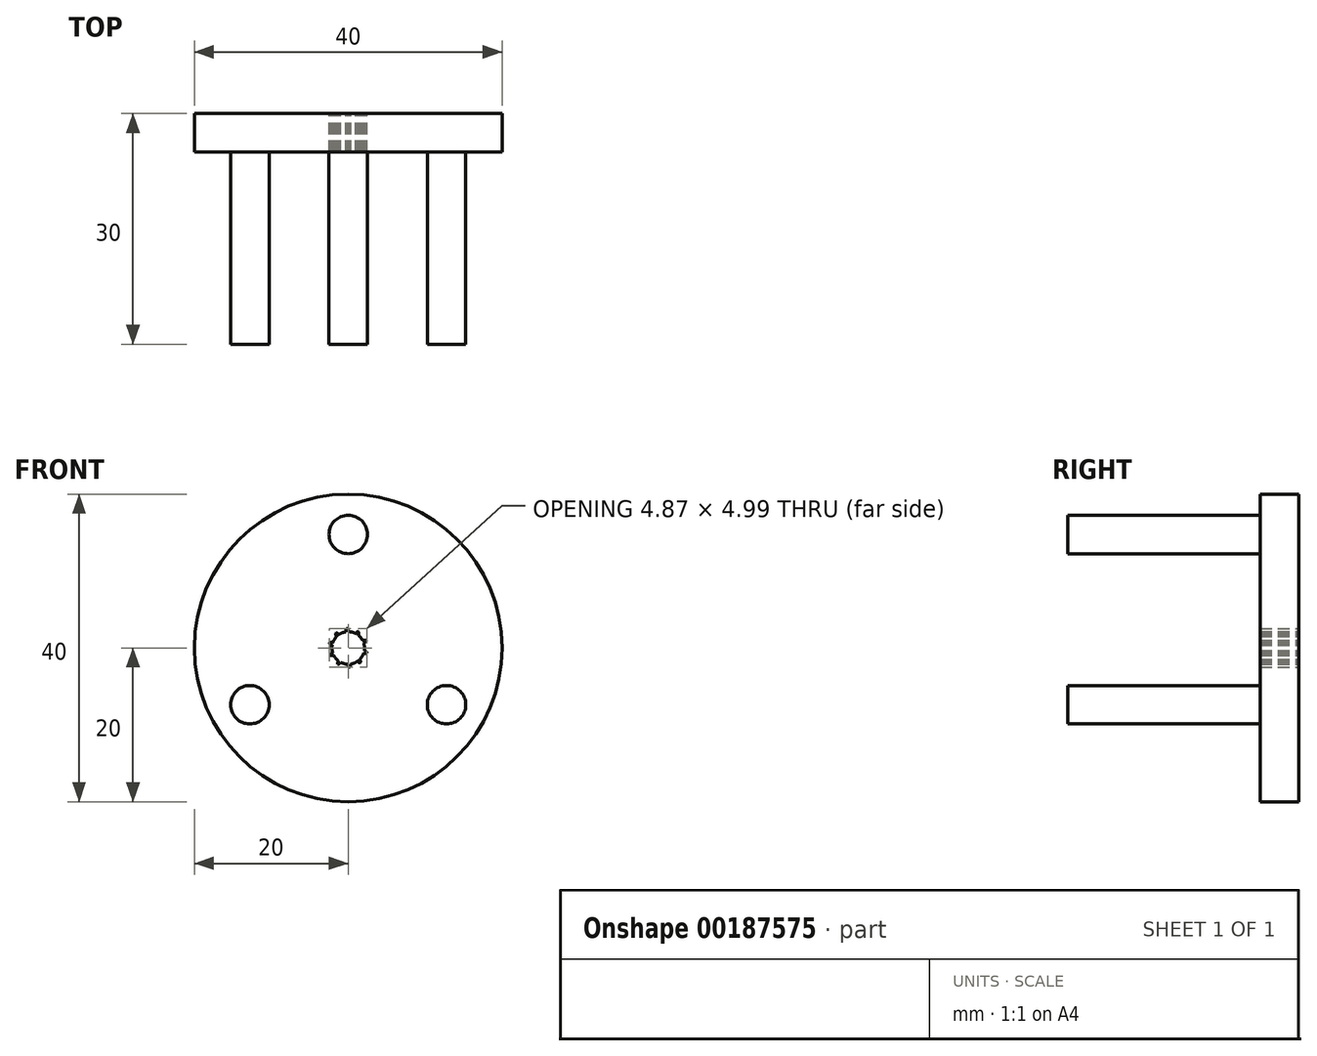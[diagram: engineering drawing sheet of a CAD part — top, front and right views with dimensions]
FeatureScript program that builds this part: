
annotation { "Feature Type Name" : "Feature", "Feature Type Description" : "" }
export const myFeature = defineFeature(function(context is Context, id is Id, definition is map)
    precondition{}
    {
        {
            var Q0;
            Q0=qCreatedBy(makeId("Front.planeOp"),FACE);
            var sketch = newSketch(context, id + "F0", { "sketchPlane" : qUnion([Q0])});
            skCircle(sketch, "E0", {"center": v(0, 0) * mm, "radius": 20 * mm});
            skCircle(sketch, "E1", {"center": v(0, 0) * mm, "radius": 2.12 * mm});
            skCircle(sketch, "E2", {"center": v(0, 0) * mm, "radius": 2.31 * mm, "construction": true});
            skCircle(sketch, "E3", {"center": v(0, 0) * mm, "radius": 2.5 * mm, "construction": true});
            skLineSegment(sketch, "E4", {"start": v(0, 0) * mm, "end": v(0, 3) * mm, "construction": true});
            skLineSegment(sketch, "E5", {"start": v(0, 0) * mm, "end": v(-0.2, 3) * mm, "construction": true});
            skLineSegment(sketch, "E6", {"start": v(0, 2.31) * mm, "end": v(-2.48, 2.31) * mm, "construction": true});
            skLineSegment(sketch, "E7", {"start": v(0, 2.31) * mm, "end": v(-2.45, 1.42) * mm, "construction": true});
            skCircle(sketch, "E8", {"center": v(0, 2.31) * mm, "radius": 0.57 * mm, "construction": true});
            skCircle(sketch, "E9", {"center": v(0, 0) * mm, "radius": 2.17 * mm, "construction": true});
            skCircle(sketch, "E10", {"center": v(-0.54, 2.1) * mm, "radius": 0.57 * mm, "construction": true});
            skArc(sketch, "E11", {"start": v(0, 2.31) * mm, "mid": v(-0.05, 2.4) * mm, "end": v(-0.12, 2.5) * mm});
            skArc(sketch, "E12", {"start": v(0.04, 2.11) * mm, "mid": v(0.03, 2.21) * mm, "end": v(0, 2.31) * mm});
            skArc(sketch, "E13.MirrorCS", {"start": v(-0.3, 2.3) * mm, "mid": v(-0.27, 2.4) * mm, "end": v(-0.2, 2.5) * mm});
            skArc(sketch, "E14.MirrorCS", {"start": v(-0.31, 2.1) * mm, "mid": v(-0.32, 2.2) * mm, "end": v(-0.3, 2.3) * mm});
            skLineSegment(sketch, "E15", {"start": v(-0.2, 2.5) * mm, "end": v(-0.12, 2.5) * mm});
            skArc(sketch, "E16.1.0", {"start": v(1.1, 2.03) * mm, "mid": v(1.2, 2.1) * mm, "end": v(1.3, 2.14) * mm});
            skArc(sketch, "E16.1.1", {"start": v(0.98, 1.88) * mm, "mid": v(1.03, 1.96) * mm, "end": v(1.1, 2.03) * mm});
            skLineSegment(sketch, "E16.1.2", {"start": v(1.3, 2.14) * mm, "end": v(1.37, 2.09) * mm});
            skArc(sketch, "E16.1.3", {"start": v(1.36, 1.87) * mm, "mid": v(1.38, 1.98) * mm, "end": v(1.37, 2.09) * mm});
            skArc(sketch, "E16.1.4", {"start": v(1.27, 1.69) * mm, "mid": v(1.32, 1.77) * mm, "end": v(1.36, 1.87) * mm});
            skArc(sketch, "E16.2.0", {"start": v(2.08, 1) * mm, "mid": v(2.2, 1) * mm, "end": v(2.3, 0.97) * mm});
            skArc(sketch, "E16.2.1", {"start": v(1.9, 0.94) * mm, "mid": v(1.99, 0.98) * mm, "end": v(2.08, 1) * mm});
            skLineSegment(sketch, "E16.2.2", {"start": v(2.3, 0.97) * mm, "end": v(2.34, 0.88) * mm});
            skArc(sketch, "E16.2.3", {"start": v(2.2, 0.71) * mm, "mid": v(2.28, 0.8) * mm, "end": v(2.34, 0.88) * mm});
            skArc(sketch, "E16.2.4", {"start": v(2.02, 0.62) * mm, "mid": v(2.11, 0.66) * mm, "end": v(2.2, 0.71) * mm});
            skArc(sketch, "E16.3.0", {"start": v(2.27, -0.42) * mm, "mid": v(2.36, -0.49) * mm, "end": v(2.43, -0.57) * mm});
            skArc(sketch, "E16.3.1", {"start": v(2.09, -0.35) * mm, "mid": v(2.18, -0.38) * mm, "end": v(2.27, -0.42) * mm});
            skLineSegment(sketch, "E16.3.2", {"start": v(2.43, -0.57) * mm, "end": v(2.41, -0.66) * mm});
            skArc(sketch, "E16.3.3", {"start": v(2.2, -0.71) * mm, "mid": v(2.3, -0.7) * mm, "end": v(2.41, -0.66) * mm});
            skArc(sketch, "E16.3.4", {"start": v(2, -0.69) * mm, "mid": v(2.1, -0.71) * mm, "end": v(2.2, -0.71) * mm});
            skArc(sketch, "E16.4.0", {"start": v(1.6, -1.68) * mm, "mid": v(1.62, -1.78) * mm, "end": v(1.63, -1.9) * mm});
            skArc(sketch, "E16.4.1", {"start": v(1.48, -1.5) * mm, "mid": v(1.54, -1.59) * mm, "end": v(1.6, -1.68) * mm});
            skLineSegment(sketch, "E16.4.2", {"start": v(1.63, -1.9) * mm, "end": v(1.56, -1.95) * mm});
            skArc(sketch, "E16.4.3", {"start": v(1.36, -1.87) * mm, "mid": v(1.46, -1.92) * mm, "end": v(1.56, -1.95) * mm});
            skArc(sketch, "E16.4.4", {"start": v(1.21, -1.73) * mm, "mid": v(1.28, -1.8) * mm, "end": v(1.36, -1.87) * mm});
            skArc(sketch, "E16.5.0", {"start": v(0.3, -2.3) * mm, "mid": v(0.27, -2.4) * mm, "end": v(0.2, -2.5) * mm});
            skArc(sketch, "E16.5.1", {"start": v(0.31, -2.1) * mm, "mid": v(0.32, -2.2) * mm, "end": v(0.3, -2.3) * mm});
            skLineSegment(sketch, "E16.5.2", {"start": v(0.2, -2.5) * mm, "end": v(0.12, -2.5) * mm});
            skArc(sketch, "E16.5.3", {"start": v(0, -2.31) * mm, "mid": v(0.05, -2.4) * mm, "end": v(0.12, -2.5) * mm});
            skArc(sketch, "E16.5.4", {"start": v(-0.04, -2.11) * mm, "mid": v(-0.03, -2.21) * mm, "end": v(0, -2.31) * mm});
            skArc(sketch, "E16.6.0", {"start": v(-1.1, -2.03) * mm, "mid": v(-1.2, -2.1) * mm, "end": v(-1.3, -2.14) * mm});
            skArc(sketch, "E16.6.1", {"start": v(-0.98, -1.88) * mm, "mid": v(-1.03, -1.96) * mm, "end": v(-1.1, -2.03) * mm});
            skLineSegment(sketch, "E16.6.2", {"start": v(-1.3, -2.14) * mm, "end": v(-1.37, -2.09) * mm});
            skArc(sketch, "E16.6.3", {"start": v(-1.36, -1.87) * mm, "mid": v(-1.38, -1.98) * mm, "end": v(-1.37, -2.09) * mm});
            skArc(sketch, "E16.6.4", {"start": v(-1.27, -1.69) * mm, "mid": v(-1.32, -1.77) * mm, "end": v(-1.36, -1.87) * mm});
            skArc(sketch, "E16.7.0", {"start": v(-2.08, -1) * mm, "mid": v(-2.2, -1) * mm, "end": v(-2.3, -0.97) * mm});
            skArc(sketch, "E16.7.1", {"start": v(-1.9, -0.94) * mm, "mid": v(-1.99, -0.98) * mm, "end": v(-2.08, -1) * mm});
            skLineSegment(sketch, "E16.7.2", {"start": v(-2.3, -0.97) * mm, "end": v(-2.34, -0.88) * mm});
            skArc(sketch, "E16.7.3", {"start": v(-2.2, -0.71) * mm, "mid": v(-2.28, -0.8) * mm, "end": v(-2.34, -0.88) * mm});
            skArc(sketch, "E16.7.4", {"start": v(-2.02, -0.62) * mm, "mid": v(-2.11, -0.66) * mm, "end": v(-2.2, -0.71) * mm});
            skArc(sketch, "E16.8.0", {"start": v(-2.27, 0.42) * mm, "mid": v(-2.36, 0.49) * mm, "end": v(-2.43, 0.57) * mm});
            skArc(sketch, "E16.8.1", {"start": v(-2.09, 0.35) * mm, "mid": v(-2.18, 0.38) * mm, "end": v(-2.27, 0.42) * mm});
            skLineSegment(sketch, "E16.8.2", {"start": v(-2.43, 0.57) * mm, "end": v(-2.41, 0.66) * mm});
            skArc(sketch, "E16.8.3", {"start": v(-2.2, 0.71) * mm, "mid": v(-2.3, 0.7) * mm, "end": v(-2.41, 0.66) * mm});
            skArc(sketch, "E16.8.4", {"start": v(-2, 0.69) * mm, "mid": v(-2.1, 0.71) * mm, "end": v(-2.2, 0.71) * mm});
            skArc(sketch, "E16.9.0", {"start": v(-1.6, 1.68) * mm, "mid": v(-1.62, 1.78) * mm, "end": v(-1.63, 1.9) * mm});
            skArc(sketch, "E16.9.1", {"start": v(-1.48, 1.5) * mm, "mid": v(-1.54, 1.59) * mm, "end": v(-1.6, 1.68) * mm});
            skLineSegment(sketch, "E16.9.2", {"start": v(-1.63, 1.9) * mm, "end": v(-1.56, 1.95) * mm});
            skArc(sketch, "E16.9.3", {"start": v(-1.36, 1.87) * mm, "mid": v(-1.46, 1.92) * mm, "end": v(-1.56, 1.95) * mm});
            skArc(sketch, "E16.9.4", {"start": v(-1.21, 1.73) * mm, "mid": v(-1.28, 1.8) * mm, "end": v(-1.36, 1.87) * mm});
            skLineSegment(sketch, "E16.anchor1", {"start": v(0, 0) * mm, "end": v(-0.3, 2.3) * mm, "construction": true});
            skLineSegment(sketch, "E16.anchor2", {"start": v(0, 0) * mm, "end": v(-0.3, 2.3) * mm, "construction": true});
            skSolve(sketch);
        }
        {
            var Q0;
            Q0 = qSketchRegion(id + "F0", true);
            extrude(context, id + "F1", {"entities" : qUnion([Q0]), "depth" : 5 * mm});
        }
        {
            var Q0;
            Q0=makeQuery(id+"F1.opExtrude","CAP_FACE",FACE,{"disambiguationData":[OSD([sQuery(id+"F0.wireOp",EDGE,"E0"),sQuery(id+"F0.wireOp",EDGE,"E1"),sQuery(id+"F0.wireOp",EDGE,"E16.1.0"),sQuery(id+"F0.wireOp",EDGE,"E16.1.1"),sQuery(id+"F0.wireOp",EDGE,"E16.1.2"),sQuery(id+"F0.wireOp",EDGE,"E16.1.3"),sQuery(id+"F0.wireOp",EDGE,"E16.1.4"),sQuery(id+"F0.wireOp",EDGE,"E16.2.0"),sQuery(id+"F0.wireOp",EDGE,"E16.2.1"),sQuery(id+"F0.wireOp",EDGE,"E16.2.2"),sQuery(id+"F0.wireOp",EDGE,"E16.2.3"),sQuery(id+"F0.wireOp",EDGE,"E16.2.4"),sQuery(id+"F0.wireOp",EDGE,"E16.3.0"),sQuery(id+"F0.wireOp",EDGE,"E16.3.1"),sQuery(id+"F0.wireOp",EDGE,"E16.3.2"),sQuery(id+"F0.wireOp",EDGE,"E16.3.3"),sQuery(id+"F0.wireOp",EDGE,"E16.3.4"),sQuery(id+"F0.wireOp",EDGE,"E16.4.0"),sQuery(id+"F0.wireOp",EDGE,"E16.4.1"),sQuery(id+"F0.wireOp",EDGE,"E16.4.2"),sQuery(id+"F0.wireOp",EDGE,"E16.4.3"),sQuery(id+"F0.wireOp",EDGE,"E16.4.4"),sQuery(id+"F0.wireOp",EDGE,"E16.5.0"),sQuery(id+"F0.wireOp",EDGE,"E16.5.1"),sQuery(id+"F0.wireOp",EDGE,"E16.5.2"),sQuery(id+"F0.wireOp",EDGE,"E16.5.3"),sQuery(id+"F0.wireOp",EDGE,"E16.5.4"),sQuery(id+"F0.wireOp",EDGE,"E16.6.0"),sQuery(id+"F0.wireOp",EDGE,"E16.6.1"),sQuery(id+"F0.wireOp",EDGE,"E16.6.2"),sQuery(id+"F0.wireOp",EDGE,"E16.6.3"),sQuery(id+"F0.wireOp",EDGE,"E16.6.4"),sQuery(id+"F0.wireOp",EDGE,"E16.7.0"),sQuery(id+"F0.wireOp",EDGE,"E16.7.1"),sQuery(id+"F0.wireOp",EDGE,"E16.7.2"),sQuery(id+"F0.wireOp",EDGE,"E16.7.3"),sQuery(id+"F0.wireOp",EDGE,"E16.7.4"),sQuery(id+"F0.wireOp",EDGE,"E16.8.0"),sQuery(id+"F0.wireOp",EDGE,"E16.8.1"),sQuery(id+"F0.wireOp",EDGE,"E16.8.2"),sQuery(id+"F0.wireOp",EDGE,"E16.8.3"),sQuery(id+"F0.wireOp",EDGE,"E16.8.4"),sQuery(id+"F0.wireOp",EDGE,"E16.9.0"),sQuery(id+"F0.wireOp",EDGE,"E16.9.1"),sQuery(id+"F0.wireOp",EDGE,"E16.9.2"),sQuery(id+"F0.wireOp",EDGE,"E16.9.3"),sQuery(id+"F0.wireOp",EDGE,"E16.9.4"),sQuery(id+"F0.wireOp",EDGE,"E13.MirrorCS"),sQuery(id+"F0.wireOp",EDGE,"E14.MirrorCS"),sQuery(id+"F0.wireOp",EDGE,"E15"),sQuery(id+"F0.wireOp",EDGE,"E11"),sQuery(id+"F0.wireOp",EDGE,"E12")])],"isStart":false});
            var sketch = newSketch(context, id + "F2", { "sketchPlane" : qUnion([Q0])});
            skCircle(sketch, "E17", {"center": v(0, 14.76) * mm, "radius": 2.5 * mm});
            skCircle(sketch, "E18.1.0", {"center": v(-12.78, -7.38) * mm, "radius": 2.5 * mm});
            skCircle(sketch, "E18.2.0", {"center": v(12.78, -7.38) * mm, "radius": 2.5 * mm});
            skPoint(sketch, "E18.center", {"position": v(0, 0) * mm});
            skSolve(sketch);
        }
        {
            var Q0;
            Q0 = qSketchRegion(id + "F2", true);
            extrude(context, id + "F3", {"entities" : qUnion([Q0]), "operationType" : NewBodyOperationType.ADD, "depth" : 25 * mm});
        }
    });
